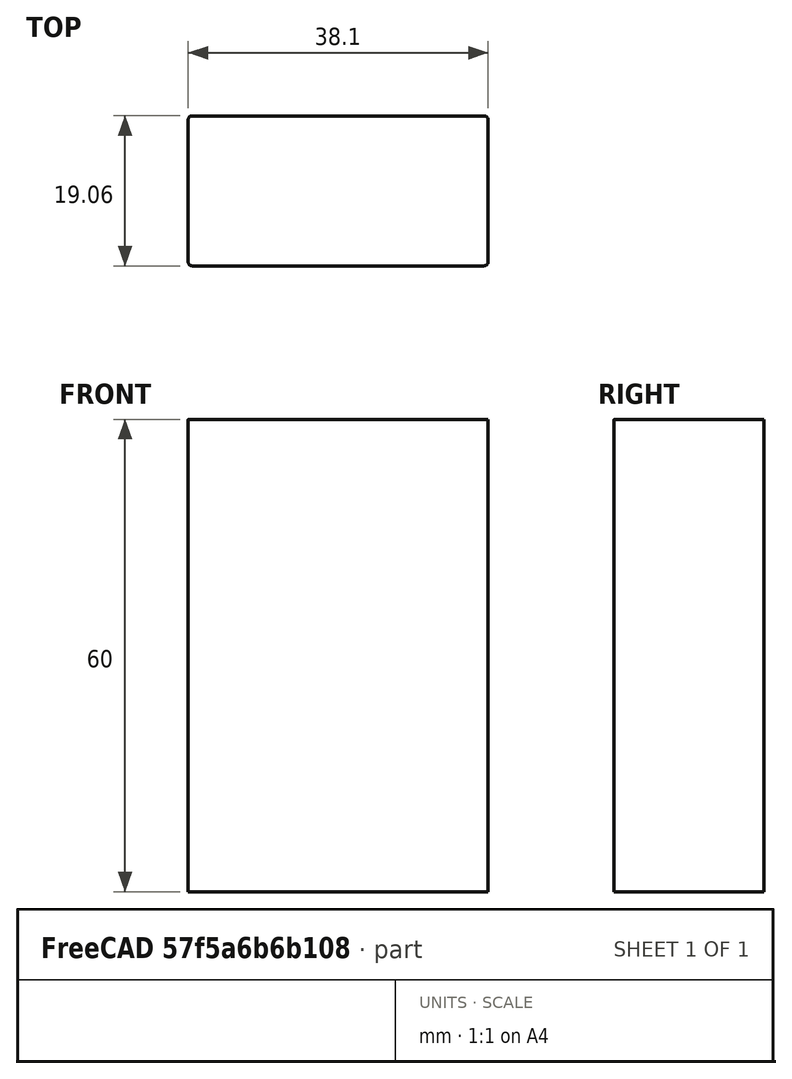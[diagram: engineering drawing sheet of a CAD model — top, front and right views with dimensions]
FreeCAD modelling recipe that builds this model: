
FCSTD DOCUMENT  (FreeCAD 0.20R29177 +426 (Git))
Label: Board
License: All rights reserved
LicenseURL: http://en.wikipedia.org/wiki/All_rights_reserved
objects: PartDesign::CoordinateSystem×3, Sketcher::SketchObject×1, App::FeaturePython×1, PartDesign::Pad×1, PartDesign::Body×1, App::Part×1
note: 7 computed .brp shape members not serialized (recipe doc carries the construction recipe); baked Part::Feature solids carry a one-line shape summary decoded from their .brp

FEATURE [Sketcher::SketchObject] Sketch
  FullyConstrained = true
  MapMode = 5
  Support = -> [XY_Plane001]
  expr: Constraints[16] = <<Variables>>.FilletRadius
  expr: Constraints[18] = <<Variables>>.Dim1
  expr: Constraints[19] = <<Variables>>.Dim2
  sketch-geometry (9):
    g0: LineSegment StartX=-19.05 StartY=9.025 StartZ=0 EndX=-19.05 EndY=-9.025 EndZ=0
    g1: LineSegment StartX=-18.55 StartY=-9.525 StartZ=0 EndX=18.55 EndY=-9.525 EndZ=0
    g2: LineSegment StartX=19.05 StartY=-9.025 StartZ=0 EndX=19.05 EndY=9.025 EndZ=0
    g3: LineSegment StartX=18.55 StartY=9.525 StartZ=0 EndX=-18.55 EndY=9.525 EndZ=0
    g4: GeomPoint X=0 Y=0 Z=0
    g5: ArcOfCircle CenterX=-18.55 CenterY=9.025 CenterZ=0 NormalX=0 NormalY=0 NormalZ=1 AngleXU=0 Radius=0.5 StartAngle=1.5708 EndAngle=3.14159
    g6: ArcOfCircle CenterX=-18.55 CenterY=-9.025 CenterZ=0 NormalX=0 NormalY=0 NormalZ=1 AngleXU=0 Radius=0.5 StartAngle=3.14159 EndAngle=4.71239
    g7: ArcOfCircle CenterX=18.55 CenterY=9.025 CenterZ=0 NormalX=0 NormalY=0 NormalZ=1 AngleXU=0 Radius=0.5 StartAngle=-8.4555e-12 EndAngle=1.5708
    g8: ArcOfCircle CenterX=18.55 CenterY=-9.025 CenterZ=0 NormalX=0 NormalY=0 NormalZ=1 AngleXU=0 Radius=0.5 StartAngle=4.71239 EndAngle=6.28319
  constraints (20):
    c: Horizontal(g1)
    c: Horizontal(g3)
    c: Vertical(g0)
    c: Vertical(g2)
    c: Coincident(g4,g-1)
    c: Tangent(g3,g5) = -1.5708
    c: Tangent(g0,g5) = -1.5708
    c: Tangent(g0,g6) = -1.5708
    c: Tangent(g1,g6) = -1.5708
    c: Tangent(g3,g7) = -1.5708
    c: Tangent(g2,g7) = -1.5708
    c: Tangent(g2,g8) = -1.5708
    c: Tangent(g1,g8) = -1.5708
    c: Equal(g8,g7)
    c: Equal(g7,g5)
    c: Equal(g5,g6)
    c: Radius(g7) = 0.5
    c: Symmetric(g7,g6,g4)
    c: DistanceY(g1,g3) = 19.05
    c: DistanceX(g0,g2) = 38.1
FEATURE [App::FeaturePython] Variables  # WARN: FeaturePython — macro-defined, semantics opaque (R4)
  Dim1 = 19.05
  Dim2 = 38.1
  FilletRadius = 0.5
  Length = 60
  Type = App::PropertyContainer
FEATURE [PartDesign::Pad] Pad
  Direction = (0,0,1)
  Length = 60
  Length2 = 10
  Midplane = true
  Profile = -> Sketch
  ReferenceAxis = -> Sketch [N_Axis]
  Type = 0
  expr: Length = <<Variables>>.Length
FEATURE [PartDesign::Body] Body
  Group = -> [Sketch,Pad]
  Origin = -> Origin001
  Tip = -> Pad
FEATURE [PartDesign::CoordinateSystem] LCS_Center
  AttacherType = Attacher::AttachEngine3D
  MapMode = 2
  Support = -> [XY_Plane]
FEATURE [PartDesign::CoordinateSystem] LCS_End1
  AttacherType = Attacher::AttachEngine3D
  AttachmentOffset = pos=(0,0,30) rot=(0,0,1;0rad)
  MapMode = 2
  Placement = pos=(0,0,30) rot=(0,0,1;0rad)
  Support = -> [XY_Plane]
  expr: .AttachmentOffset.Base.z = <<Variables>>.Length / 2
FEATURE [PartDesign::CoordinateSystem] LCS_End2
  AttacherType = Attacher::AttachEngine3D
  AttachmentOffset = pos=(0,0,-30) rot=(0,0,1;0rad)
  MapMode = 2
  Placement = pos=(0,0,-30) rot=(0,0,1;0rad)
  Support = -> [XY_Plane]
  expr: .AttachmentOffset.Base.z = <<Variables>>.Length / -2
FEATURE [App::Part] Part
  Group = -> [Body,Variables,LCS_Center,LCS_End1,LCS_End2]
  Origin = -> Origin
  Type = Asm4::VariantLink
